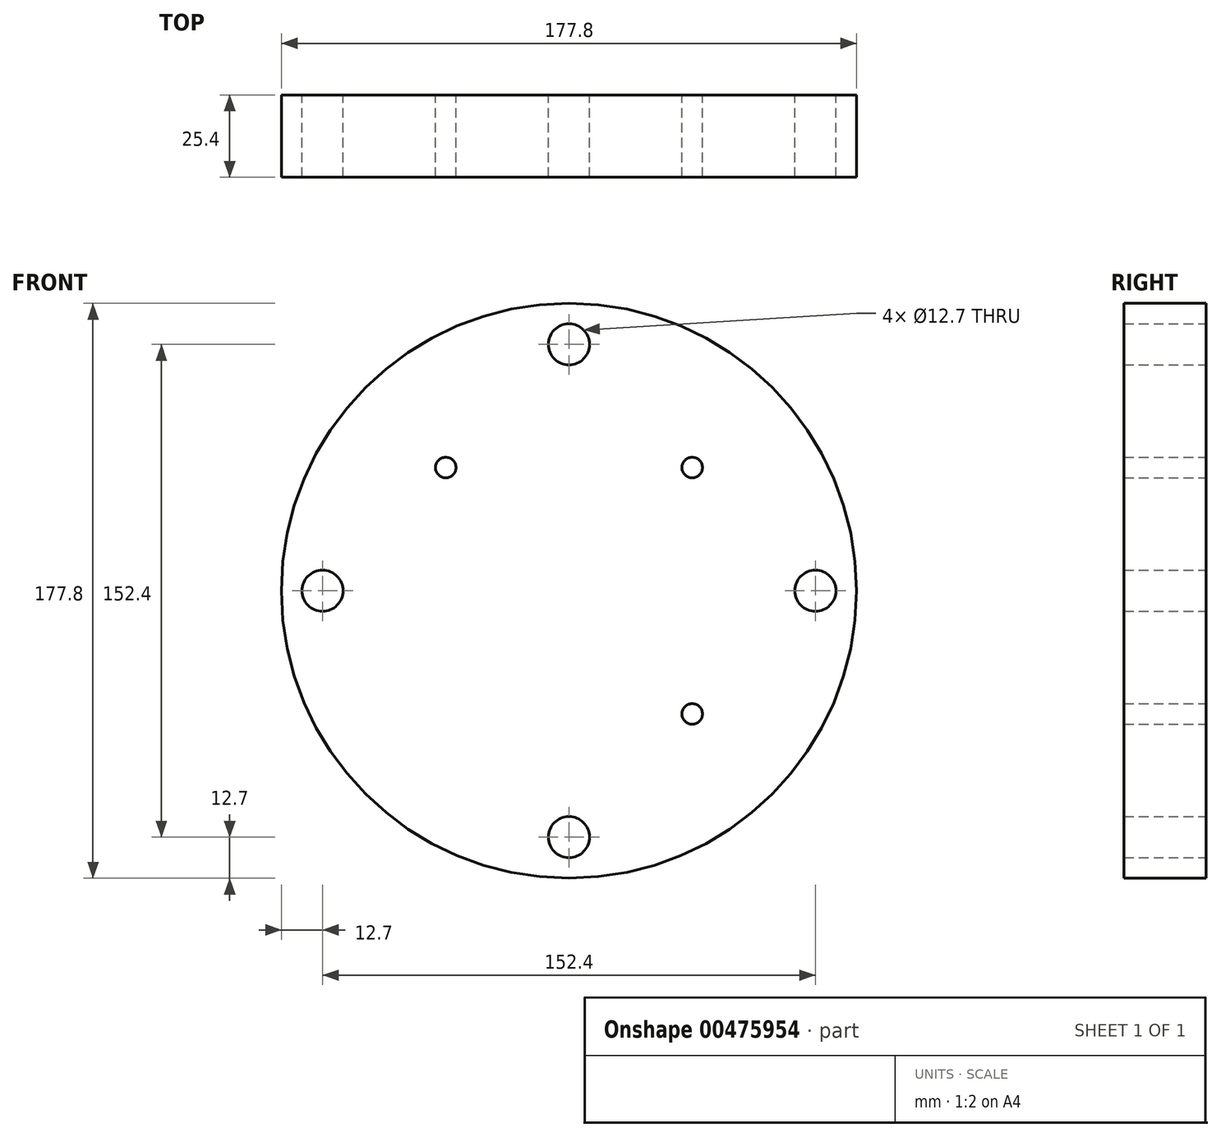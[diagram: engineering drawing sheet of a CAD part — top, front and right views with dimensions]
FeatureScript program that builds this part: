
annotation { "Feature Type Name" : "Feature", "Feature Type Description" : "" }
export const myFeature = defineFeature(function(context is Context, id is Id, definition is map)
    precondition{}
    {
        {
            var Q0;
            Q0=qCreatedBy(makeId("Front.planeOp"),FACE);
            var sketch = newSketch(context, id + "F0", { "sketchPlane" : qUnion([Q0])});
            skCircle(sketch, "E0", {"center": v(0, 0) * mm, "radius": 88.9 * mm});
            skCircle(sketch, "E1", {"center": v(0, -76.2) * mm, "radius": 6.35 * mm});
            skCircle(sketch, "E2", {"center": v(76.2, 0) * mm, "radius": 6.35 * mm});
            skCircle(sketch, "E3", {"center": v(-76.2, 0) * mm, "radius": 6.35 * mm});
            skCircle(sketch, "E4", {"center": v(0, 76.2) * mm, "radius": 6.35 * mm});
            skPoint(sketch, "E5", {"position": v(38.1, 38.1) * mm});
            skCircle(sketch, "E6", {"center": v(38.1, 38.1) * mm, "radius": 3.18 * mm});
            skPoint(sketch, "E7", {"position": v(-38.1, 38.1) * mm});
            skPoint(sketch, "E8", {"position": v(38.1, -38.1) * mm});
            skCircle(sketch, "E9", {"center": v(-38.1, 38.1) * mm, "radius": 3.18 * mm});
            skCircle(sketch, "E10", {"center": v(38.1, -38.1) * mm, "radius": 3.18 * mm});
            skSolve(sketch);
        }
        {
            var Q0;
            Q0=makeQuery(id+"F0.imprint","IMPRINT",FACE,{"disambiguationData":[TD([[makeQuery(id+"F0.imprint","IMPRINT",EDGE,{"derivedFrom":sQuery(id+"F0.wireOp",EDGE,"E0")}),1.0]])]});
            var Q1;
            Q1=sQuery(id+"F0.wireOp",EDGE,"E0");
            extrude(context, id + "F1", {"entities" : qUnion([Q0]), "surfaceEntities" : qUnion([Q1]), "depth" : 25.4 * mm});
        }
    });
